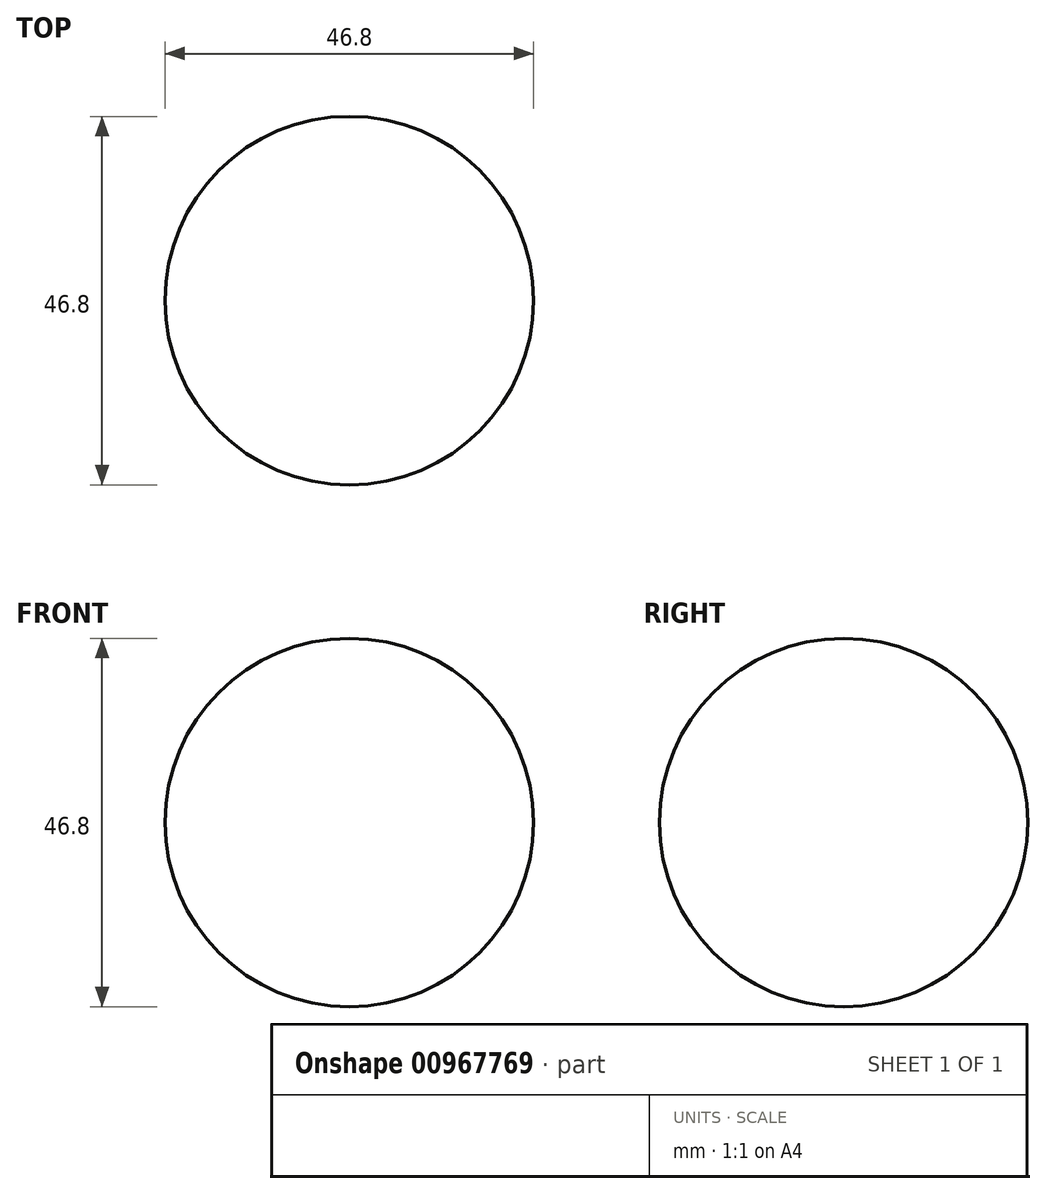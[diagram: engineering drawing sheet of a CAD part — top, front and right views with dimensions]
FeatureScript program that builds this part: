
annotation { "Feature Type Name" : "Feature", "Feature Type Description" : "" }
export const myFeature = defineFeature(function(context is Context, id is Id, definition is map)
    precondition{}
    {
        {
            var Q0;
            Q0=qCreatedBy(makeId("Front.planeOp"),FACE);
            var sketch = newSketch(context, id + "F0", { "sketchPlane" : qUnion([Q0])});
            skCircle(sketch, "E0", {"center": v(0, 0) * mm, "radius": 23.4 * mm});
            skLineSegment(sketch, "E1", {"start": v(0, 23.4) * mm, "end": v(0, -23.4) * mm});
            skSolve(sketch);
        }
        {
            var Q0;
            {var subQ0=sQuery(id+"F0.wireOp",EDGE,"E1");Q0=makeQuery(id+"F0.imprint","IMPRINT",FACE,{"disambiguationData":[TD([[makeQuery(id+"F0.imprint","IMPRINT",EDGE,{"derivedFrom":subQ0}),1.0]])]});}
            var Q1;
            Q1=sQuery(id+"F0.wireOp",EDGE,"E1");
            revolve(context, id + "F1", {"surfaceOperationType" : NewSurfaceOperationType.NEW, "entities" : qUnion([Q0]), "axis" : qUnion([Q1]), "revolveType" : RevolveType.FULL});
        }
    });
